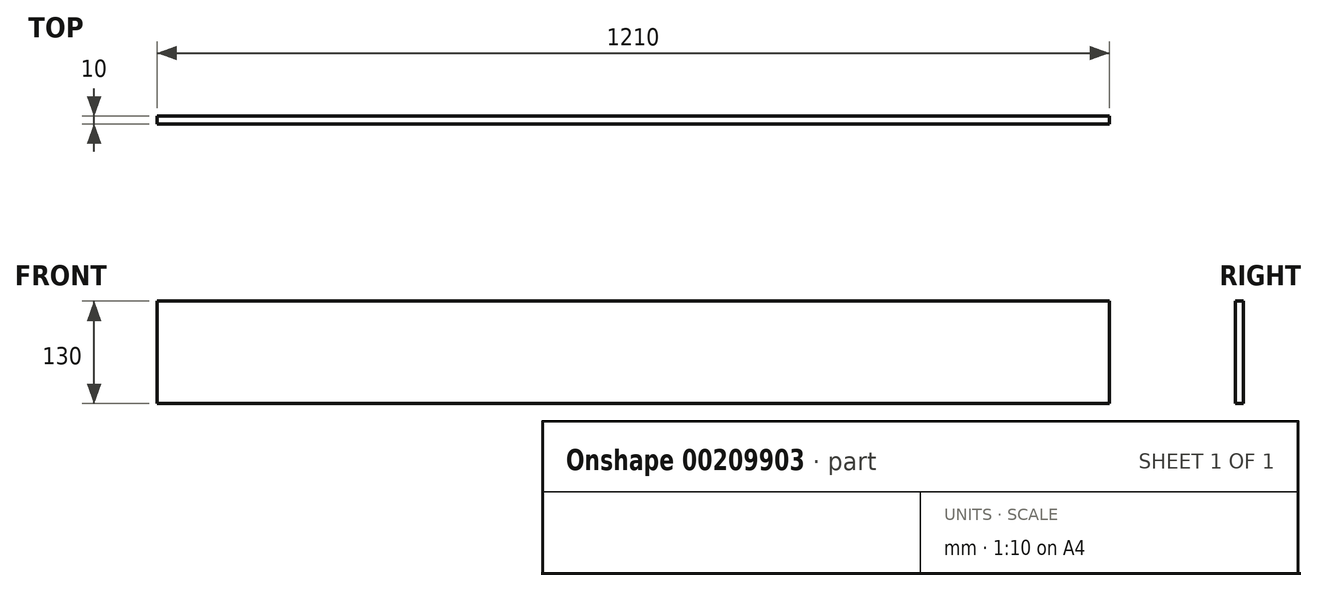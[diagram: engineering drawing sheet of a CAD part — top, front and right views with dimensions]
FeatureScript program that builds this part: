
annotation { "Feature Type Name" : "Feature", "Feature Type Description" : "" }
export const myFeature = defineFeature(function(context is Context, id is Id, definition is map)
    precondition{}
    {
        {
            var Q0;
            Q0=qCreatedBy(makeId("Front.planeOp"),FACE);
            var sketch = newSketch(context, id + "F0", { "sketchPlane" : qUnion([Q0])});
            skLineSegment(sketch, "E0.bottom", {"start": v(-605, 65) * mm, "end": v(605, 65) * mm});
            skLineSegment(sketch, "E0.top", {"start": v(-605, -65) * mm, "end": v(605, -65) * mm});
            skLineSegment(sketch, "E0.left", {"start": v(-605, 65) * mm, "end": v(-605, -65) * mm});
            skLineSegment(sketch, "E0.right", {"start": v(605, 65) * mm, "end": v(605, -65) * mm});
            skPoint(sketch, "E0.middle", {"position": v(0, 0) * mm});
            skSolve(sketch);
        }
        {
            var Q0;
            Q0=makeQuery(id+"F0.imprint","IMPRINT",FACE,{"disambiguationData":[TD([[makeQuery(id+"F0.imprint","IMPRINT",EDGE,{"derivedFrom":sQuery(id+"F0.wireOp",EDGE,"E0.bottom")}),-1.0]])]});
            extrude(context, id + "F1", {"entities" : qUnion([Q0]), "depth" : 10 * mm});
        }
    });
